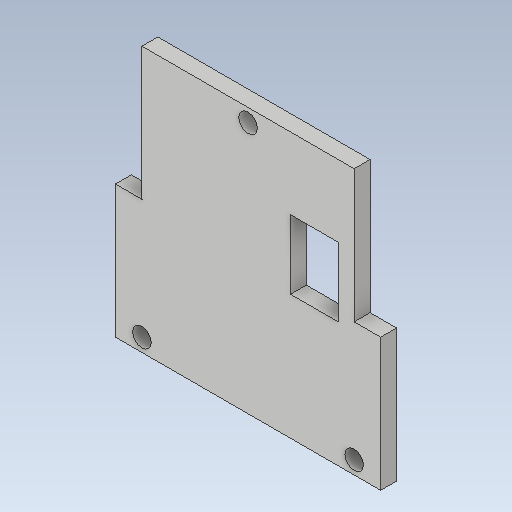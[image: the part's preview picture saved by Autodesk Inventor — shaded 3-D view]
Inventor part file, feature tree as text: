
AUTODESK INVENTOR PART (.ipt)
format: ipt  version: 2020.1 (Build 241239000, 239)  size: 132,608 bytes
history: native  units: mm
features: extrude x2, sketch x2
ambient origin geometry x8: Origin, YZ Plane, XZ Plane, XY Plane, X Axis, Y Axis, Z Axis, Center Point
bodies: Solid1 (feature_tree)
feature tree (4):
  extrude  "Extrusion1"  Depth=50.0mm
  extrude  "Extrusion2"  Depth=5.0mm
  sketch  "Sketch1"  dims[d0=50.0mm d1=50.0mm]
  sketch  "Sketch2"  dims[d2=2.5mm d3=5.0mm d4=2.5mm d5=5.0mm d6=2.5mm d7=3.5mm d8=3.5mm d9=3.5mm d10=3.0mm d11=0.0mm d12=5.0mm d13=25.0mm d14=25.0mm d15=5.0mm d16=3.0mm d17=0.0mm d18=13.0mm d19=20.0mm d20=4.0mm d21=6.5mm d22=9.0mm d23=13.0mm d24=9.0mm]
